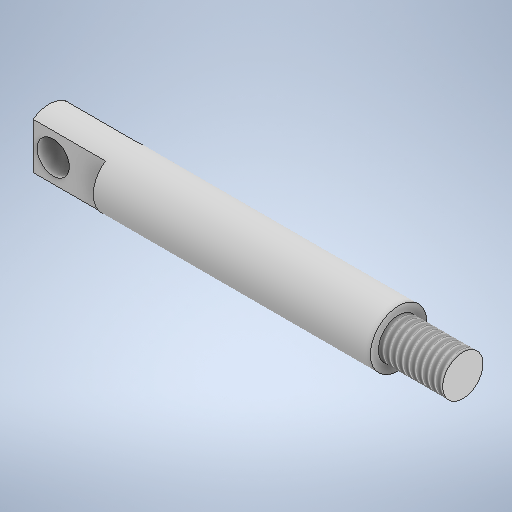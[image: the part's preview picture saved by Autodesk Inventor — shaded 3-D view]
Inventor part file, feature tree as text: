
AUTODESK INVENTOR PART (.ipt)
format: ipt  version: 2025.1 (Build 291241000, 241)  size: 287,744 bytes
history: native  units: mm
features: sketch x3, revolve x1, thread x1, extrude x1, hole x1
ambient origin geometry x8: Origin, YZ Plane, XZ Plane, XY Plane, X Axis, Y Axis, Z Axis, Center Point
bodies: Solid1 (feature_tree)
feature tree (7):
  revolve  "Revolution1"  [1 undecoded]
  thread  "Thread1"  [1 undecoded]
  extrude  "Extrusion1"  Depth=11.0mm TaperAngle=0.0deg
  hole  "Hole1"  [1 undecoded]
  sketch  "Sketch1"  dims[d0=5.0mm d1=7.0mm d2=8.0mm]
  sketch  "Sketch3"  dims[d3=90.0deg d4=11.0mm d5=0.0mm]
  sketch  "Sketch4"  dims[d7=2.0mm d8=2.0mm d9=9.0mm d10=0.0mm d11=2.5mm d12=4.0mm d13=9.0mm d14=4.0mm d15=2.0mm d16=90.0deg d17=9.0mm d18=0.0mm d19=43.5mm]
note: 3 required parameter values undecoded (feature->parameter linkage not recoverable at this tier; creation-order binding heuristic only, values carry confidence <= 0.55)